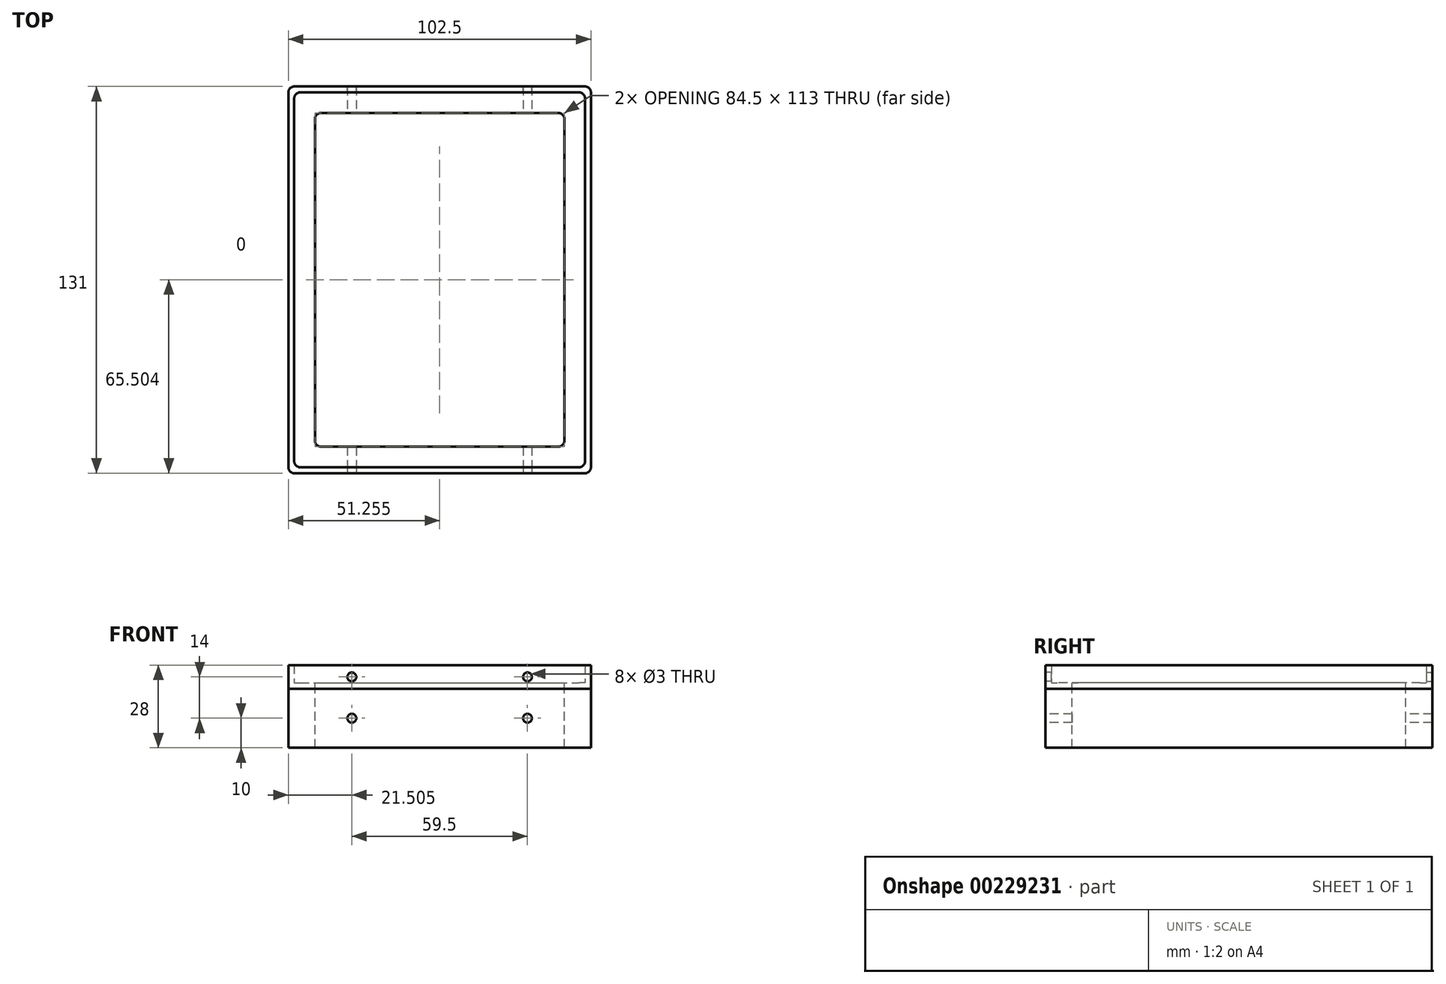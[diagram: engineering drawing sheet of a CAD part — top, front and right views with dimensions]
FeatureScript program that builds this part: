
annotation { "Feature Type Name" : "Feature", "Feature Type Description" : "" }
export const myFeature = defineFeature(function(context is Context, id is Id, definition is map)
    precondition{}
    {
        {
            var Q0;
            Q0=qCreatedBy(makeId("Top.planeOp"),FACE);
            var sketch = newSketch(context, id + "F0", { "sketchPlane" : qUnion([Q0])});
            skLineSegment(sketch, "E0.bottom", {"start": v(-48.46, 61.26) * mm, "end": v(46.04, 61.26) * mm});
            skLineSegment(sketch, "E0.top", {"start": v(-48.46, -65.74) * mm, "end": v(46.04, -65.74) * mm});
            skLineSegment(sketch, "E0.left", {"start": v(-50.46, 59.26) * mm, "end": v(-50.46, -63.74) * mm});
            skLineSegment(sketch, "E0.right", {"start": v(48.04, 59.26) * mm, "end": v(48.04, -63.74) * mm});
            skLineSegment(sketch, "E1.bottom", {"start": v(-50.46, 63.26) * mm, "end": v(48.04, 63.26) * mm});
            skLineSegment(sketch, "E1.top", {"start": v(-50.46, -67.74) * mm, "end": v(48.04, -67.74) * mm});
            skLineSegment(sketch, "E1.left", {"start": v(-52.46, 61.26) * mm, "end": v(-52.46, -65.74) * mm});
            skLineSegment(sketch, "E1.right", {"start": v(50.04, 61.26) * mm, "end": v(50.04, -65.74) * mm});
            skPoint(sketch, "E2.visualSharp", {"position": v(48.04, 61.26) * mm});
            skArc(sketch, "E2.filletArc", {"start": v(48.04, 59.26) * mm, "mid": v(47.46, 60.68) * mm, "end": v(46.04, 61.26) * mm});
            skPoint(sketch, "E3.visualSharp", {"position": v(50.04, 63.26) * mm});
            skArc(sketch, "E3.filletArc", {"start": v(50.04, 61.26) * mm, "mid": v(49.46, 62.68) * mm, "end": v(48.04, 63.26) * mm});
            skPoint(sketch, "E4.visualSharp", {"position": v(-50.46, 61.26) * mm});
            skArc(sketch, "E4.filletArc", {"start": v(-48.46, 61.26) * mm, "mid": v(-49.87, 60.68) * mm, "end": v(-50.46, 59.26) * mm});
            skPoint(sketch, "E5.visualSharp", {"position": v(-52.46, 63.26) * mm});
            skArc(sketch, "E5.filletArc", {"start": v(-50.46, 63.26) * mm, "mid": v(-51.87, 62.68) * mm, "end": v(-52.46, 61.26) * mm});
            skPoint(sketch, "E6.visualSharp", {"position": v(48.04, -65.74) * mm});
            skArc(sketch, "E6.filletArc", {"start": v(46.04, -65.74) * mm, "mid": v(47.46, -65.15) * mm, "end": v(48.04, -63.74) * mm});
            skPoint(sketch, "E7.visualSharp", {"position": v(50.04, -67.74) * mm});
            skArc(sketch, "E7.filletArc", {"start": v(48.04, -67.74) * mm, "mid": v(49.46, -67.15) * mm, "end": v(50.04, -65.74) * mm});
            skPoint(sketch, "E8.visualSharp", {"position": v(-50.46, -65.74) * mm});
            skArc(sketch, "E8.filletArc", {"start": v(-50.46, -63.74) * mm, "mid": v(-49.87, -65.15) * mm, "end": v(-48.46, -65.74) * mm});
            skPoint(sketch, "E9.visualSharp", {"position": v(-52.46, -67.74) * mm});
            skArc(sketch, "E9.filletArc", {"start": v(-52.46, -65.74) * mm, "mid": v(-51.87, -67.15) * mm, "end": v(-50.46, -67.74) * mm});
            skSolve(sketch);
        }
        {
            var Q0;
            Q0=qSketchRegion(id+"F0",true);
            extrude(context, id + "F1", {"entities" : qUnion([Q0]), "depth" : 6 * mm});
        }
        {
            var Q0;
            Q0=qCreatedBy(makeId("Top.planeOp"),FACE);
            var sketch = newSketch(context, id + "F2", { "sketchPlane" : qUnion([Q0])});
            skLineSegment(sketch, "E10.bottom", {"start": v(-50.46, 63.26) * mm, "end": v(48.04, 63.26) * mm});
            skLineSegment(sketch, "E10.top", {"start": v(-50.46, -67.74) * mm, "end": v(48.04, -67.74) * mm});
            skLineSegment(sketch, "E10.left", {"start": v(-52.46, 61.26) * mm, "end": v(-52.46, -65.74) * mm});
            skLineSegment(sketch, "E10.right", {"start": v(50.04, 61.26) * mm, "end": v(50.04, -65.74) * mm});
            skLineSegment(sketch, "E11.bottom", {"start": v(-41.46, 54.26) * mm, "end": v(39.04, 54.26) * mm});
            skLineSegment(sketch, "E11.top", {"start": v(-41.46, -58.74) * mm, "end": v(39.04, -58.74) * mm});
            skLineSegment(sketch, "E11.left", {"start": v(-43.46, 52.26) * mm, "end": v(-43.46, -56.74) * mm});
            skLineSegment(sketch, "E11.right", {"start": v(41.04, 52.26) * mm, "end": v(41.04, -56.74) * mm});
            skPoint(sketch, "E12.visualSharp", {"position": v(-43.46, -58.74) * mm});
            skArc(sketch, "E12.filletArc", {"start": v(-43.46, -56.74) * mm, "mid": v(-42.87, -58.15) * mm, "end": v(-41.46, -58.74) * mm});
            skPoint(sketch, "E13.visualSharp", {"position": v(41.04, -58.74) * mm});
            skArc(sketch, "E13.filletArc", {"start": v(39.04, -58.74) * mm, "mid": v(40.46, -58.15) * mm, "end": v(41.04, -56.74) * mm});
            skPoint(sketch, "E14.visualSharp", {"position": v(41.04, 54.26) * mm});
            skArc(sketch, "E14.filletArc", {"start": v(41.04, 52.26) * mm, "mid": v(40.46, 53.68) * mm, "end": v(39.04, 54.26) * mm});
            skPoint(sketch, "E15.visualSharp", {"position": v(-43.46, 54.26) * mm});
            skArc(sketch, "E15.filletArc", {"start": v(-41.46, 54.26) * mm, "mid": v(-42.87, 53.68) * mm, "end": v(-43.46, 52.26) * mm});
            skPoint(sketch, "E16.visualSharp", {"position": v(-52.46, -67.74) * mm});
            skArc(sketch, "E16.filletArc", {"start": v(-52.46, -65.74) * mm, "mid": v(-51.87, -67.15) * mm, "end": v(-50.46, -67.74) * mm});
            skPoint(sketch, "E17.visualSharp", {"position": v(50.04, -67.74) * mm});
            skArc(sketch, "E17.filletArc", {"start": v(48.04, -67.74) * mm, "mid": v(49.46, -67.15) * mm, "end": v(50.04, -65.74) * mm});
            skPoint(sketch, "E18.visualSharp", {"position": v(50.04, 63.26) * mm});
            skArc(sketch, "E18.filletArc", {"start": v(50.04, 61.26) * mm, "mid": v(49.46, 62.68) * mm, "end": v(48.04, 63.26) * mm});
            skPoint(sketch, "E19.visualSharp", {"position": v(-52.46, 63.26) * mm});
            skArc(sketch, "E19.filletArc", {"start": v(-50.46, 63.26) * mm, "mid": v(-51.87, 62.68) * mm, "end": v(-52.46, 61.26) * mm});
            skSolve(sketch);
        }
        {
            var Q0;
            Q0=qSketchRegion(id+"F2",true);
            extrude(context, id + "F3", {"entities" : qUnion([Q0]), "operationType" : NewBodyOperationType.ADD, "oppositeDirection" : true, "depth" : 2 * mm});
        }
        {
            var Q0;
            Q0=makeQuery(id+"F3.boolean.opBoolean","MERGE",FACE,{"derivedFrom":[makeQuery(id+"F1.opExtrude","SWEPT_FACE",FACE,{"disambiguationData":[OSD([sQuery(id+"F0.wireOp",EDGE,"E1.top")])]}),makeQuery(id+"F3.opExtrude","SWEPT_FACE",FACE,{"disambiguationData":[OSD([sQuery(id+"F2.wireOp",EDGE,"E10.top")])]})]});
            var sketch = newSketch(context, id + "F4", { "sketchPlane" : qUnion([Q0])});
            skCircle(sketch, "E20", {"center": v(28.54, 2) * mm, "radius": 1.5 * mm});
            skCircle(sketch, "E21", {"center": v(-30.96, 2) * mm, "radius": 1.5 * mm});
            skSolve(sketch);
        }
        {
            var Q0;
            Q0=makeQuery(id+"F3.boolean.opBoolean","MERGE",FACE,{"derivedFrom":[makeQuery(id+"F1.opExtrude","SWEPT_FACE",FACE,{"disambiguationData":[OSD([sQuery(id+"F0.wireOp",EDGE,"E1.bottom")])]}),makeQuery(id+"F3.opExtrude","SWEPT_FACE",FACE,{"disambiguationData":[OSD([sQuery(id+"F2.wireOp",EDGE,"E10.bottom")])]})]});
            var sketch = newSketch(context, id + "F5", { "sketchPlane" : qUnion([Q0])});
            skCircle(sketch, "E22", {"center": v(-28.54, 2) * mm, "radius": 1.5 * mm});
            skCircle(sketch, "E23", {"center": v(30.96, 2) * mm, "radius": 1.5 * mm});
            skSolve(sketch);
        }
        {
            var Q0;
            Q0=qSketchRegion(id+"F4",true);
            extrude(context, id + "F6", {"entities" : qUnion([Q0]), "operationType" : NewBodyOperationType.REMOVE, "oppositeDirection" : true, "depth" : 2 * mm});
        }
        {
            var Q0;
            Q0=qSketchRegion(id+"F5",true);
            extrude(context, id + "F7", {"entities" : qUnion([Q0]), "operationType" : NewBodyOperationType.REMOVE, "oppositeDirection" : true, "depth" : 2 * mm});
        }
        {
            var Q0;
            Q0=makeQuery(id+"F3.opExtrude","CAP_FACE",FACE,{"disambiguationData":[OSD([sQuery(id+"F2.wireOp",EDGE,"E10.bottom"),sQuery(id+"F2.wireOp",EDGE,"E10.top"),sQuery(id+"F2.wireOp",EDGE,"E10.left"),sQuery(id+"F2.wireOp",EDGE,"E10.right"),sQuery(id+"F2.wireOp",EDGE,"E11.bottom"),sQuery(id+"F2.wireOp",EDGE,"E11.top"),sQuery(id+"F2.wireOp",EDGE,"E11.left"),sQuery(id+"F2.wireOp",EDGE,"E11.right"),sQuery(id+"F2.wireOp",EDGE,"E12.filletArc"),sQuery(id+"F2.wireOp",EDGE,"E13.filletArc"),sQuery(id+"F2.wireOp",EDGE,"E14.filletArc"),sQuery(id+"F2.wireOp",EDGE,"E15.filletArc"),sQuery(id+"F2.wireOp",EDGE,"E16.filletArc"),sQuery(id+"F2.wireOp",EDGE,"E17.filletArc"),sQuery(id+"F2.wireOp",EDGE,"E18.filletArc"),sQuery(id+"F2.wireOp",EDGE,"E19.filletArc")])],"isStart":false});
            extrude(context, id + "F8", {"entities" : qUnion([Q0]), "depth" : 20 * mm});
        }
        {
            var Q0;
            Q0=makeQuery(id+"F8.opExtrude","SWEPT_FACE",FACE,{"disambiguationData":[OSD([sQuery(id+"F2.wireOp",EDGE,"E10.top")])]});
            var sketch = newSketch(context, id + "F9", { "sketchPlane" : qUnion([Q0])});
            skCircle(sketch, "E24", {"center": v(28.54, -12) * mm, "radius": 1.5 * mm});
            skCircle(sketch, "E25", {"center": v(-30.96, -12) * mm, "radius": 1.5 * mm});
            skSolve(sketch);
        }
        {
            var Q0;
            Q0=qSketchRegion(id+"F9",true);
            extrude(context, id + "F10", {"entities" : qUnion([Q0]), "operationType" : NewBodyOperationType.REMOVE, "oppositeDirection" : true, "depth" : 135 * mm});
        }
    });
